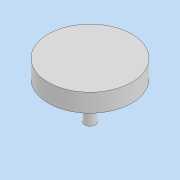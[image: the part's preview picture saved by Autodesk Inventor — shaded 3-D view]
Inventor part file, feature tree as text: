
AUTODESK INVENTOR PART (.ipt)
format: ipt  version: 2022 (Build 260153070, 153G)  size: 103,936 bytes
history: native  units: mm
features: revolve x1, sketch x1
ambient origin geometry x8: Origin, YZ Plane, XZ Plane, XY Plane, X Axis, Y Axis, Z Axis, Center Point
bodies: Solid1 (feature_tree)
feature tree (2):
  revolve  "Revolution1"  [1 undecoded]
  sketch  "Sketch1"  dims[d0=2.9mm d1=11.0mm d2=11.34464mm d4=10.0mm d5=90.0deg d6=23.0mm]
note: 1 required parameter value undecoded (feature->parameter linkage not recoverable at this tier; creation-order binding heuristic only, values carry confidence <= 0.55)
